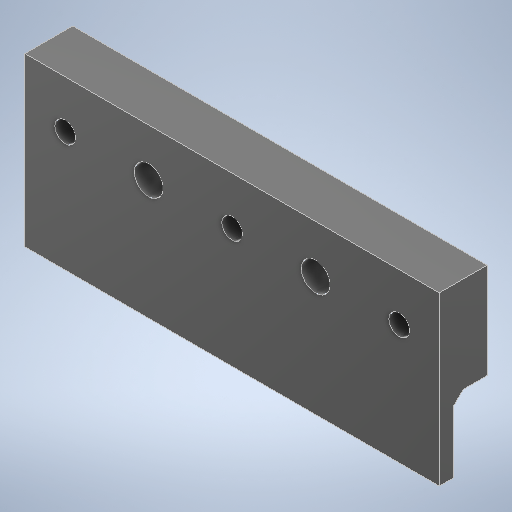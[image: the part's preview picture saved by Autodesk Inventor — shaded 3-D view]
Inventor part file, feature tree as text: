
AUTODESK INVENTOR PART (.ipt)
format: ipt  version: 2025.1 (Build 291241020, 241B)  size: 493,056 bytes
history: native  units: mm
features: sketch x7, extrude x5, hole x2, plane x2, projected_geometry x2, other x2, pattern_linear x1, chamfer x1, reference x1
ambient origin geometry x8: Origin, YZ Plane, XZ Plane, XY Plane, X Axis, Y Axis, Z Axis, Center Point
bodies: Solid1 (feature_tree)
feature tree (23):
  extrude  "Extrusion1"  Depth=20.0mm
  sketch  "Sketch2"  dims[d2=3.0mm d3=0.0mm d5=25.4mm]
  extrude  "Extrusion3"  Depth=3.0mm
  hole  "Hole2"  [1 undecoded]
  hole  "Hole3"  [1 undecoded]
  pattern_linear  "Rectangular Pattern2"  Spacing1=34.925mm  [1 undecoded]
  chamfer  "Chamfer1"  Distance=34.925mm
  extrude  "Extrusion4"  Depth=5.0mm
  plane  "Work Plane1"
  plane  "Work Plane2"
  extrude  "Extrusion5"  Depth=5.0mm
  extrude  "Extrusion6"  Depth=10.0mm
  sketch  "Sketch1"  dims[d0=260.0mm d1=20.0mm]
  reference  "Reference1"
  sketch  "Sketch5"  dims[d6=12.7mm d31=10.0mm]
  sketch  "Sketch6"  dims[d32=20.0mm d33=10.0mm d34=0.0mm]
  sketch  "Sketch7"  dims[d35=42.6875mm]
  sketch  "Sketch8"  dims[d39=6.0mm d40=6.0mm d41=4.0mm d42=2.0mm d43=90.0deg d44=8.0mm d45=20.594885mm]
  projected_geometry  "Projected Loop1"
  sketch  "Sketch9"  dims[d46=42.6875mm d47=34.925mm d48=34.925mm d49=34.925mm d50=34.925mm d51=10.0mm d52=4.3mm d53=6.0mm d54=4.0mm d55=2.0mm d56=90.0deg d57=6.0mm d58=0.0mm d59=70.0mm d61=34.925mm d62=10.0mm d63=2.0mm d64=2.0mm d65=45.0deg d66=5.0mm d67=0.0mm d68=0.0mm d69=-86.666667mm d70=-173.333333mm d71=0.0mm d72=0.0mm d73=0.0mm d74=0.0mm]
  projected_geometry  "Projected Loop2"
  other  "MagDrop4.iam"
  other  "Connect4_RACK:1"
note: 3 required parameter values undecoded (feature->parameter linkage not recoverable at this tier; creation-order binding heuristic only, values carry confidence <= 0.55)
